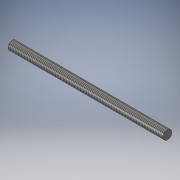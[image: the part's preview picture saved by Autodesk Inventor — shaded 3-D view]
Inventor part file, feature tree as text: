
AUTODESK INVENTOR PART (.ipt)
format: ipt  version: 2018 (Build 220112000, 112)  size: 100,864 bytes
history: native  units: in
note: dims shown in document units (in); Inventor stores cm internally (conversion verified against a paired STEP export)
features: extrude x1, chamfer x1, thread x1, sketch x1
ambient origin geometry x8: Origin, YZ Plane, XZ Plane, XY Plane, X Axis, Y Axis, Z Axis, Center Point
bodies: Solid1 (feature_tree)
feature tree (4):
  extrude  "Extrusion1"  Depth=2.7559in TaperAngle=0.0deg
  chamfer  "Chamfer1"  Distance=0.0787in Angle=45.0deg
  thread  "Thread1"  [1 undecoded]
  sketch  "Sketch1"  dims[d0=0.1575in d1=2.7559in d2=0.0in d3=0.0039in d4=0.0787in d5=45.0deg d6=0.3937in d7=0.0in]
note: 1 required parameter value undecoded (feature->parameter linkage not recoverable at this tier; creation-order binding heuristic only, values carry confidence <= 0.55)
